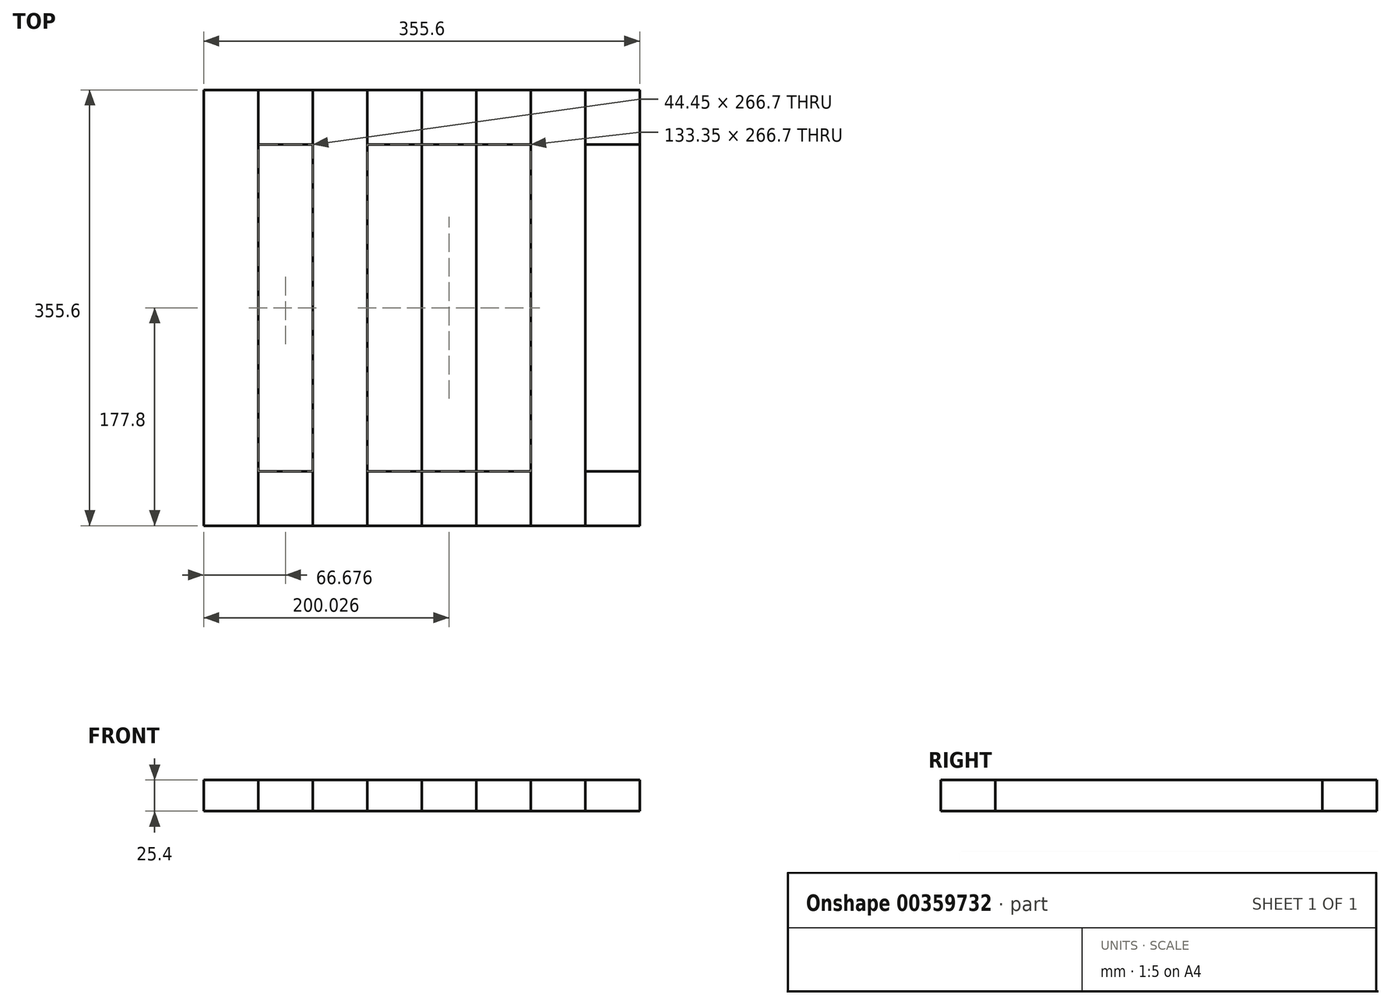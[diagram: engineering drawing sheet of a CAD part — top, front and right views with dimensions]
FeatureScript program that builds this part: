
annotation { "Feature Type Name" : "Feature", "Feature Type Description" : "" }
export const myFeature = defineFeature(function(context is Context, id is Id, definition is map)
    precondition{}
    {
        {
            var Q0;
            Q0=qCreatedBy(makeId("Top.planeOp"),FACE);
            var sketch = newSketch(context, id + "F0", { "sketchPlane" : qUnion([Q0])});
            skLineSegment(sketch, "E0.bottom", {"start": v(181.84, 177.8) * mm, "end": v(-173.76, 177.8) * mm});
            skLineSegment(sketch, "E0.top", {"start": v(181.84, -177.8) * mm, "end": v(-173.76, -177.8) * mm});
            skLineSegment(sketch, "E0.left", {"start": v(181.84, 177.8) * mm, "end": v(181.84, -177.8) * mm});
            skLineSegment(sketch, "E0.right", {"start": v(-173.76, 177.8) * mm, "end": v(-173.76, -177.8) * mm});
            skPoint(sketch, "E0.middle", {"position": v(4.04, 0) * mm});
            skLineSegment(sketch, "E1", {"start": v(-129.3, 177.8) * mm, "end": v(-129.3, -177.8) * mm});
            skLineSegment(sketch, "E2", {"start": v(-84.86, -177.8) * mm, "end": v(-84.86, 177.8) * mm});
            skLineSegment(sketch, "E3", {"start": v(-40.4, -177.8) * mm, "end": v(-40.4, 177.8) * mm});
            skLineSegment(sketch, "E4", {"start": v(4.04, 177.8) * mm, "end": v(4.04, -177.8) * mm});
            skLineSegment(sketch, "E5", {"start": v(4.04, -177.8) * mm, "end": v(4.04, 177.8) * mm});
            skLineSegment(sketch, "E6.MirrorCS", {"start": v(48.5, -177.8) * mm, "end": v(48.5, 177.8) * mm});
            skLineSegment(sketch, "E7.MirrorCS", {"start": v(92.94, -177.8) * mm, "end": v(92.94, 177.8) * mm});
            skLineSegment(sketch, "E8.MirrorCS", {"start": v(137.4, 177.8) * mm, "end": v(137.4, -177.8) * mm});
            skLineSegment(sketch, "E9", {"start": v(4.04, 0) * mm, "end": v(-173.76, 0) * mm});
            skLineSegment(sketch, "E10", {"start": v(-173.76, 0) * mm, "end": v(181.84, 0) * mm});
            skLineSegment(sketch, "E11", {"start": v(-173.76, 44.45) * mm, "end": v(181.84, 44.45) * mm});
            skLineSegment(sketch, "E12", {"start": v(181.84, 88.9) * mm, "end": v(-173.76, 88.9) * mm});
            skLineSegment(sketch, "E13", {"start": v(-173.76, 133.35) * mm, "end": v(181.84, 133.35) * mm});
            skLineSegment(sketch, "E14.MirrorCS", {"start": v(-173.76, -44.45) * mm, "end": v(181.84, -44.45) * mm});
            skLineSegment(sketch, "E15.MirrorCS", {"start": v(181.84, -88.9) * mm, "end": v(-173.76, -88.9) * mm});
            skLineSegment(sketch, "E16.MirrorCS", {"start": v(-173.76, -133.35) * mm, "end": v(181.84, -133.35) * mm});
            skSolve(sketch);
        }
        {
            var Q0;
            {var subQ0=sQuery(id+"F0.wireOp",EDGE,"E0.right");var subQ1=sQuery(id+"F0.wireOp",EDGE,"E0.bottom");var subQ2=makeQuery(id+"F0.imprint","INTERSECT",VERTEX,{"derivedFrom":[subQ1,subQ0]});Q0=makeQuery(id+"F0.imprint","IMPRINT",FACE,{"disambiguationData":[TD([[makeQuery(id+"F0.imprint","IMPRINT",EDGE,{"disambiguationData":[TD([[subQ2,1.0]])],"derivedFrom":subQ1}),1.0]])]});}
            var Q1;
            {var subQ0=sQuery(id+"F0.wireOp",EDGE,"E12");var subQ1=sQuery(id+"F0.wireOp",EDGE,"E0.right");var subQ2=makeQuery(id+"F0.imprint","INTERSECT",VERTEX,{"derivedFrom":[subQ1,subQ0]});Q1=makeQuery(id+"F0.imprint","IMPRINT",FACE,{"disambiguationData":[TD([[makeQuery(id+"F0.imprint","IMPRINT",EDGE,{"disambiguationData":[TD([[subQ2,1.0]])],"derivedFrom":subQ1}),1.0]])]});}
            var Q2;
            {var subQ0=sQuery(id+"F0.wireOp",EDGE,"E11");var subQ1=sQuery(id+"F0.wireOp",EDGE,"E0.right");var subQ2=makeQuery(id+"F0.imprint","INTERSECT",VERTEX,{"derivedFrom":[subQ1,subQ0]});Q2=makeQuery(id+"F0.imprint","IMPRINT",FACE,{"disambiguationData":[TD([[makeQuery(id+"F0.imprint","IMPRINT",EDGE,{"disambiguationData":[TD([[subQ2,1.0]])],"derivedFrom":subQ1}),1.0]])]});}
            var Q3;
            {var subQ0=sQuery(id+"F0.wireOp",EDGE,"E10");var subQ1=sQuery(id+"F0.wireOp",EDGE,"E0.right");var subQ2=makeQuery(id+"F0.imprint","INTERSECT",VERTEX,{"derivedFrom":[subQ1,subQ0]});Q3=makeQuery(id+"F0.imprint","IMPRINT",FACE,{"disambiguationData":[TD([[makeQuery(id+"F0.imprint","IMPRINT",EDGE,{"disambiguationData":[TD([[subQ2,-1.0]])],"derivedFrom":subQ1}),1.0]])]});}
            var Q4;
            {var subQ0=sQuery(id+"F0.wireOp",EDGE,"E14.MirrorCS");var subQ1=sQuery(id+"F0.wireOp",EDGE,"E0.right");var subQ2=makeQuery(id+"F0.imprint","INTERSECT",VERTEX,{"derivedFrom":[subQ1,subQ0]});Q4=makeQuery(id+"F0.imprint","IMPRINT",FACE,{"disambiguationData":[TD([[makeQuery(id+"F0.imprint","IMPRINT",EDGE,{"disambiguationData":[TD([[subQ2,-1.0]])],"derivedFrom":subQ1}),1.0]])]});}
            var Q5;
            {var subQ0=sQuery(id+"F0.wireOp",EDGE,"E10");var subQ1=sQuery(id+"F0.wireOp",EDGE,"E0.right");var subQ2=makeQuery(id+"F0.imprint","INTERSECT",VERTEX,{"derivedFrom":[subQ1,subQ0]});Q5=makeQuery(id+"F0.imprint","IMPRINT",FACE,{"disambiguationData":[TD([[makeQuery(id+"F0.imprint","IMPRINT",EDGE,{"disambiguationData":[TD([[subQ2,1.0]])],"derivedFrom":subQ1}),1.0]])]});}
            var Q6;
            {var subQ0=sQuery(id+"F0.wireOp",EDGE,"E15.MirrorCS");var subQ1=sQuery(id+"F0.wireOp",EDGE,"E0.right");var subQ2=makeQuery(id+"F0.imprint","INTERSECT",VERTEX,{"derivedFrom":[subQ1,subQ0]});Q6=makeQuery(id+"F0.imprint","IMPRINT",FACE,{"disambiguationData":[TD([[makeQuery(id+"F0.imprint","IMPRINT",EDGE,{"disambiguationData":[TD([[subQ2,-1.0]])],"derivedFrom":subQ1}),1.0]])]});}
            var Q7;
            {var subQ0=sQuery(id+"F0.wireOp",EDGE,"E0.right");var subQ1=sQuery(id+"F0.wireOp",EDGE,"E0.top");var subQ2=makeQuery(id+"F0.imprint","INTERSECT",VERTEX,{"derivedFrom":[subQ1,subQ0]});Q7=makeQuery(id+"F0.imprint","IMPRINT",FACE,{"disambiguationData":[TD([[makeQuery(id+"F0.imprint","IMPRINT",EDGE,{"disambiguationData":[TD([[subQ2,1.0]])],"derivedFrom":subQ1}),-1.0]])]});}
            var Q8;
            {var subQ0=sQuery(id+"F0.wireOp",EDGE,"E2");var subQ1=sQuery(id+"F0.wireOp",EDGE,"E0.top");var subQ2=makeQuery(id+"F0.imprint","INTERSECT",VERTEX,{"derivedFrom":[subQ1,subQ0]});Q8=makeQuery(id+"F0.imprint","IMPRINT",FACE,{"disambiguationData":[TD([[makeQuery(id+"F0.imprint","IMPRINT",EDGE,{"disambiguationData":[TD([[subQ2,1.0]])],"derivedFrom":subQ1}),-1.0]])]});}
            var Q9;
            {var subQ0=sQuery(id+"F0.wireOp",EDGE,"E16.MirrorCS");var subQ1=sQuery(id+"F0.wireOp",EDGE,"E2");var subQ2=makeQuery(id+"F0.imprint","INTERSECT",VERTEX,{"derivedFrom":[subQ1,subQ0]});Q9=makeQuery(id+"F0.imprint","IMPRINT",FACE,{"disambiguationData":[TD([[makeQuery(id+"F0.imprint","IMPRINT",EDGE,{"disambiguationData":[TD([[subQ2,-1.0]])],"derivedFrom":subQ1}),-1.0]])]});}
            var Q10;
            {var subQ0=sQuery(id+"F0.wireOp",EDGE,"E15.MirrorCS");var subQ1=sQuery(id+"F0.wireOp",EDGE,"E2");var subQ2=makeQuery(id+"F0.imprint","INTERSECT",VERTEX,{"derivedFrom":[subQ1,subQ0]});Q10=makeQuery(id+"F0.imprint","IMPRINT",FACE,{"disambiguationData":[TD([[makeQuery(id+"F0.imprint","IMPRINT",EDGE,{"disambiguationData":[TD([[subQ2,-1.0]])],"derivedFrom":subQ1}),-1.0]])]});}
            var Q11;
            {var subQ0=sQuery(id+"F0.wireOp",EDGE,"E14.MirrorCS");var subQ1=sQuery(id+"F0.wireOp",EDGE,"E2");var subQ2=makeQuery(id+"F0.imprint","INTERSECT",VERTEX,{"derivedFrom":[subQ1,subQ0]});Q11=makeQuery(id+"F0.imprint","IMPRINT",FACE,{"disambiguationData":[TD([[makeQuery(id+"F0.imprint","IMPRINT",EDGE,{"disambiguationData":[TD([[subQ2,-1.0]])],"derivedFrom":subQ1}),-1.0]])]});}
            var Q12;
            {var subQ0=sQuery(id+"F0.wireOp",EDGE,"E10");var subQ1=sQuery(id+"F0.wireOp",EDGE,"E2");var subQ2=makeQuery(id+"F0.imprint","INTERSECT",VERTEX,{"derivedFrom":[subQ1,subQ0]});Q12=makeQuery(id+"F0.imprint","IMPRINT",FACE,{"disambiguationData":[TD([[makeQuery(id+"F0.imprint","IMPRINT",EDGE,{"disambiguationData":[TD([[subQ2,-1.0]])],"derivedFrom":subQ1}),-1.0]])]});}
            var Q13;
            {var subQ0=sQuery(id+"F0.wireOp",EDGE,"E11");var subQ1=sQuery(id+"F0.wireOp",EDGE,"E2");var subQ2=makeQuery(id+"F0.imprint","INTERSECT",VERTEX,{"derivedFrom":[subQ1,subQ0]});Q13=makeQuery(id+"F0.imprint","IMPRINT",FACE,{"disambiguationData":[TD([[makeQuery(id+"F0.imprint","IMPRINT",EDGE,{"disambiguationData":[TD([[subQ2,-1.0]])],"derivedFrom":subQ1}),-1.0]])]});}
            var Q14;
            {var subQ0=sQuery(id+"F0.wireOp",EDGE,"E12");var subQ1=sQuery(id+"F0.wireOp",EDGE,"E2");var subQ2=makeQuery(id+"F0.imprint","INTERSECT",VERTEX,{"derivedFrom":[subQ1,subQ0]});Q14=makeQuery(id+"F0.imprint","IMPRINT",FACE,{"disambiguationData":[TD([[makeQuery(id+"F0.imprint","IMPRINT",EDGE,{"disambiguationData":[TD([[subQ2,-1.0]])],"derivedFrom":subQ1}),-1.0]])]});}
            var Q15;
            {var subQ0=sQuery(id+"F0.wireOp",EDGE,"E2");var subQ1=sQuery(id+"F0.wireOp",EDGE,"E0.bottom");var subQ2=makeQuery(id+"F0.imprint","INTERSECT",VERTEX,{"derivedFrom":[subQ1,subQ0]});Q15=makeQuery(id+"F0.imprint","IMPRINT",FACE,{"disambiguationData":[TD([[makeQuery(id+"F0.imprint","IMPRINT",EDGE,{"disambiguationData":[TD([[subQ2,1.0]])],"derivedFrom":subQ1}),1.0]])]});}
            var Q16;
            {var subQ0=sQuery(id+"F0.wireOp",EDGE,"E4");var subQ1=sQuery(id+"F0.wireOp",EDGE,"E0.bottom");var subQ2=makeQuery(id+"F0.imprint","INTERSECT",VERTEX,{"derivedFrom":[subQ1,subQ0]});Q16=makeQuery(id+"F0.imprint","IMPRINT",FACE,{"disambiguationData":[TD([[makeQuery(id+"F0.imprint","IMPRINT",EDGE,{"disambiguationData":[TD([[subQ2,1.0]])],"derivedFrom":subQ1}),1.0]])]});}
            var Q17;
            {var subQ0=sQuery(id+"F0.wireOp",EDGE,"E13");var subQ1=sQuery(id+"F0.wireOp",EDGE,"E4");var subQ2=makeQuery(id+"F0.imprint","INTERSECT",VERTEX,{"derivedFrom":[subQ1,subQ0]});Q17=makeQuery(id+"F0.imprint","IMPRINT",FACE,{"disambiguationData":[TD([[makeQuery(id+"F0.imprint","IMPRINT",EDGE,{"disambiguationData":[TD([[subQ2,-1.0]])],"derivedFrom":subQ1}),1.0]])]});}
            var Q18;
            {var subQ0=sQuery(id+"F0.wireOp",EDGE,"E12");var subQ1=sQuery(id+"F0.wireOp",EDGE,"E4");var subQ2=makeQuery(id+"F0.imprint","INTERSECT",VERTEX,{"derivedFrom":[subQ1,subQ0]});Q18=makeQuery(id+"F0.imprint","IMPRINT",FACE,{"disambiguationData":[TD([[makeQuery(id+"F0.imprint","IMPRINT",EDGE,{"disambiguationData":[TD([[subQ2,-1.0]])],"derivedFrom":subQ1}),1.0]])]});}
            var Q19;
            {var subQ0=sQuery(id+"F0.wireOp",EDGE,"E11");var subQ1=sQuery(id+"F0.wireOp",EDGE,"E4");var subQ2=makeQuery(id+"F0.imprint","INTERSECT",VERTEX,{"derivedFrom":[subQ1,subQ0]});Q19=makeQuery(id+"F0.imprint","IMPRINT",FACE,{"disambiguationData":[TD([[makeQuery(id+"F0.imprint","IMPRINT",EDGE,{"disambiguationData":[TD([[subQ2,-1.0]])],"derivedFrom":subQ1}),1.0]])]});}
            var Q20;
            {var subQ0=sQuery(id+"F0.wireOp",EDGE,"E10");var subQ1=sQuery(id+"F0.wireOp",EDGE,"E4");var subQ2=makeQuery(id+"F0.imprint","INTERSECT",VERTEX,{"derivedFrom":[subQ1,subQ0]});Q20=makeQuery(id+"F0.imprint","IMPRINT",FACE,{"disambiguationData":[TD([[makeQuery(id+"F0.imprint","IMPRINT",EDGE,{"disambiguationData":[TD([[subQ2,-1.0]])],"derivedFrom":subQ1}),1.0]])]});}
            var Q21;
            {var subQ0=sQuery(id+"F0.wireOp",EDGE,"E14.MirrorCS");var subQ1=sQuery(id+"F0.wireOp",EDGE,"E4");var subQ2=makeQuery(id+"F0.imprint","INTERSECT",VERTEX,{"derivedFrom":[subQ1,subQ0]});Q21=makeQuery(id+"F0.imprint","IMPRINT",FACE,{"disambiguationData":[TD([[makeQuery(id+"F0.imprint","IMPRINT",EDGE,{"disambiguationData":[TD([[subQ2,-1.0]])],"derivedFrom":subQ1}),1.0]])]});}
            var Q22;
            {var subQ0=sQuery(id+"F0.wireOp",EDGE,"E15.MirrorCS");var subQ1=sQuery(id+"F0.wireOp",EDGE,"E4");var subQ2=makeQuery(id+"F0.imprint","INTERSECT",VERTEX,{"derivedFrom":[subQ1,subQ0]});Q22=makeQuery(id+"F0.imprint","IMPRINT",FACE,{"disambiguationData":[TD([[makeQuery(id+"F0.imprint","IMPRINT",EDGE,{"disambiguationData":[TD([[subQ2,-1.0]])],"derivedFrom":subQ1}),1.0]])]});}
            var Q23;
            {var subQ0=sQuery(id+"F0.wireOp",EDGE,"E4");var subQ1=sQuery(id+"F0.wireOp",EDGE,"E0.top");var subQ2=makeQuery(id+"F0.imprint","INTERSECT",VERTEX,{"derivedFrom":[subQ1,subQ0]});Q23=makeQuery(id+"F0.imprint","IMPRINT",FACE,{"disambiguationData":[TD([[makeQuery(id+"F0.imprint","IMPRINT",EDGE,{"disambiguationData":[TD([[subQ2,1.0]])],"derivedFrom":subQ1}),-1.0]])]});}
            var Q24;
            {var subQ0=sQuery(id+"F0.wireOp",EDGE,"E7.MirrorCS");var subQ1=sQuery(id+"F0.wireOp",EDGE,"E0.top");var subQ2=makeQuery(id+"F0.imprint","INTERSECT",VERTEX,{"derivedFrom":[subQ1,subQ0]});Q24=makeQuery(id+"F0.imprint","IMPRINT",FACE,{"disambiguationData":[TD([[makeQuery(id+"F0.imprint","IMPRINT",EDGE,{"disambiguationData":[TD([[subQ2,1.0]])],"derivedFrom":subQ1}),-1.0]])]});}
            var Q25;
            {var subQ0=sQuery(id+"F0.wireOp",EDGE,"E16.MirrorCS");var subQ1=sQuery(id+"F0.wireOp",EDGE,"E7.MirrorCS");var subQ2=makeQuery(id+"F0.imprint","INTERSECT",VERTEX,{"derivedFrom":[subQ1,subQ0]});Q25=makeQuery(id+"F0.imprint","IMPRINT",FACE,{"disambiguationData":[TD([[makeQuery(id+"F0.imprint","IMPRINT",EDGE,{"disambiguationData":[TD([[subQ2,-1.0]])],"derivedFrom":subQ1}),-1.0]])]});}
            var Q26;
            {var subQ0=sQuery(id+"F0.wireOp",EDGE,"E15.MirrorCS");var subQ1=sQuery(id+"F0.wireOp",EDGE,"E7.MirrorCS");var subQ2=makeQuery(id+"F0.imprint","INTERSECT",VERTEX,{"derivedFrom":[subQ1,subQ0]});Q26=makeQuery(id+"F0.imprint","IMPRINT",FACE,{"disambiguationData":[TD([[makeQuery(id+"F0.imprint","IMPRINT",EDGE,{"disambiguationData":[TD([[subQ2,-1.0]])],"derivedFrom":subQ1}),-1.0]])]});}
            var Q27;
            {var subQ0=sQuery(id+"F0.wireOp",EDGE,"E14.MirrorCS");var subQ1=sQuery(id+"F0.wireOp",EDGE,"E7.MirrorCS");var subQ2=makeQuery(id+"F0.imprint","INTERSECT",VERTEX,{"derivedFrom":[subQ1,subQ0]});Q27=makeQuery(id+"F0.imprint","IMPRINT",FACE,{"disambiguationData":[TD([[makeQuery(id+"F0.imprint","IMPRINT",EDGE,{"disambiguationData":[TD([[subQ2,-1.0]])],"derivedFrom":subQ1}),-1.0]])]});}
            var Q28;
            {var subQ0=sQuery(id+"F0.wireOp",EDGE,"E10");var subQ1=sQuery(id+"F0.wireOp",EDGE,"E7.MirrorCS");var subQ2=makeQuery(id+"F0.imprint","INTERSECT",VERTEX,{"derivedFrom":[subQ1,subQ0]});Q28=makeQuery(id+"F0.imprint","IMPRINT",FACE,{"disambiguationData":[TD([[makeQuery(id+"F0.imprint","IMPRINT",EDGE,{"disambiguationData":[TD([[subQ2,-1.0]])],"derivedFrom":subQ1}),-1.0]])]});}
            var Q29;
            {var subQ0=sQuery(id+"F0.wireOp",EDGE,"E11");var subQ1=sQuery(id+"F0.wireOp",EDGE,"E7.MirrorCS");var subQ2=makeQuery(id+"F0.imprint","INTERSECT",VERTEX,{"derivedFrom":[subQ1,subQ0]});Q29=makeQuery(id+"F0.imprint","IMPRINT",FACE,{"disambiguationData":[TD([[makeQuery(id+"F0.imprint","IMPRINT",EDGE,{"disambiguationData":[TD([[subQ2,-1.0]])],"derivedFrom":subQ1}),-1.0]])]});}
            var Q30;
            {var subQ0=sQuery(id+"F0.wireOp",EDGE,"E12");var subQ1=sQuery(id+"F0.wireOp",EDGE,"E7.MirrorCS");var subQ2=makeQuery(id+"F0.imprint","INTERSECT",VERTEX,{"derivedFrom":[subQ1,subQ0]});Q30=makeQuery(id+"F0.imprint","IMPRINT",FACE,{"disambiguationData":[TD([[makeQuery(id+"F0.imprint","IMPRINT",EDGE,{"disambiguationData":[TD([[subQ2,-1.0]])],"derivedFrom":subQ1}),-1.0]])]});}
            var Q31;
            {var subQ0=sQuery(id+"F0.wireOp",EDGE,"E7.MirrorCS");var subQ1=sQuery(id+"F0.wireOp",EDGE,"E0.bottom");var subQ2=makeQuery(id+"F0.imprint","INTERSECT",VERTEX,{"derivedFrom":[subQ1,subQ0]});Q31=makeQuery(id+"F0.imprint","IMPRINT",FACE,{"disambiguationData":[TD([[makeQuery(id+"F0.imprint","IMPRINT",EDGE,{"disambiguationData":[TD([[subQ2,1.0]])],"derivedFrom":subQ1}),1.0]])]});}
            extrude(context, id + "F1", {"entities" : qUnion([Q0, Q1, Q2, Q3, Q4, Q5, Q6, Q7, Q8, Q9, Q10, Q11, Q12, Q13, Q14, Q15, Q16, Q17, Q18, Q19, Q20, Q21, Q22, Q23, Q24, Q25, Q26, Q27, Q28, Q29, Q30, Q31]), "depth" : 25.4 * mm});
        }
        {
            var Q0;
            {var subQ0=sQuery(id+"F0.wireOp",EDGE,"E1");var subQ1=sQuery(id+"F0.wireOp",EDGE,"E0.bottom");var subQ2=makeQuery(id+"F0.imprint","INTERSECT",VERTEX,{"derivedFrom":[subQ1,subQ0]});Q0=makeQuery(id+"F0.imprint","IMPRINT",FACE,{"disambiguationData":[TD([[makeQuery(id+"F0.imprint","IMPRINT",EDGE,{"disambiguationData":[TD([[subQ2,1.0]])],"derivedFrom":subQ1}),1.0]])]});}
            var Q1;
            {var subQ0=sQuery(id+"F0.wireOp",EDGE,"E13");var subQ1=sQuery(id+"F0.wireOp",EDGE,"E1");var subQ2=makeQuery(id+"F0.imprint","INTERSECT",VERTEX,{"derivedFrom":[subQ1,subQ0]});Q1=makeQuery(id+"F0.imprint","IMPRINT",FACE,{"disambiguationData":[TD([[makeQuery(id+"F0.imprint","IMPRINT",EDGE,{"disambiguationData":[TD([[subQ2,-1.0]])],"derivedFrom":subQ1}),1.0]])]});}
            var Q2;
            {var subQ0=sQuery(id+"F0.wireOp",EDGE,"E12");var subQ1=sQuery(id+"F0.wireOp",EDGE,"E1");var subQ2=makeQuery(id+"F0.imprint","INTERSECT",VERTEX,{"derivedFrom":[subQ1,subQ0]});Q2=makeQuery(id+"F0.imprint","IMPRINT",FACE,{"disambiguationData":[TD([[makeQuery(id+"F0.imprint","IMPRINT",EDGE,{"disambiguationData":[TD([[subQ2,-1.0]])],"derivedFrom":subQ1}),1.0]])]});}
            var Q3;
            {var subQ0=sQuery(id+"F0.wireOp",EDGE,"E11");var subQ1=sQuery(id+"F0.wireOp",EDGE,"E1");var subQ2=makeQuery(id+"F0.imprint","INTERSECT",VERTEX,{"derivedFrom":[subQ1,subQ0]});Q3=makeQuery(id+"F0.imprint","IMPRINT",FACE,{"disambiguationData":[TD([[makeQuery(id+"F0.imprint","IMPRINT",EDGE,{"disambiguationData":[TD([[subQ2,-1.0]])],"derivedFrom":subQ1}),1.0]])]});}
            var Q4;
            {var subQ0=sQuery(id+"F0.wireOp",EDGE,"E10");var subQ1=sQuery(id+"F0.wireOp",EDGE,"E1");var subQ2=makeQuery(id+"F0.imprint","INTERSECT",VERTEX,{"derivedFrom":[subQ1,subQ0]});Q4=makeQuery(id+"F0.imprint","IMPRINT",FACE,{"disambiguationData":[TD([[makeQuery(id+"F0.imprint","IMPRINT",EDGE,{"disambiguationData":[TD([[subQ2,-1.0]])],"derivedFrom":subQ1}),1.0]])]});}
            var Q5;
            {var subQ0=sQuery(id+"F0.wireOp",EDGE,"E14.MirrorCS");var subQ1=sQuery(id+"F0.wireOp",EDGE,"E1");var subQ2=makeQuery(id+"F0.imprint","INTERSECT",VERTEX,{"derivedFrom":[subQ1,subQ0]});Q5=makeQuery(id+"F0.imprint","IMPRINT",FACE,{"disambiguationData":[TD([[makeQuery(id+"F0.imprint","IMPRINT",EDGE,{"disambiguationData":[TD([[subQ2,-1.0]])],"derivedFrom":subQ1}),1.0]])]});}
            var Q6;
            {var subQ0=sQuery(id+"F0.wireOp",EDGE,"E15.MirrorCS");var subQ1=sQuery(id+"F0.wireOp",EDGE,"E1");var subQ2=makeQuery(id+"F0.imprint","INTERSECT",VERTEX,{"derivedFrom":[subQ1,subQ0]});Q6=makeQuery(id+"F0.imprint","IMPRINT",FACE,{"disambiguationData":[TD([[makeQuery(id+"F0.imprint","IMPRINT",EDGE,{"disambiguationData":[TD([[subQ2,-1.0]])],"derivedFrom":subQ1}),1.0]])]});}
            var Q7;
            {var subQ0=sQuery(id+"F0.wireOp",EDGE,"E1");var subQ1=sQuery(id+"F0.wireOp",EDGE,"E0.top");var subQ2=makeQuery(id+"F0.imprint","INTERSECT",VERTEX,{"derivedFrom":[subQ1,subQ0]});Q7=makeQuery(id+"F0.imprint","IMPRINT",FACE,{"disambiguationData":[TD([[makeQuery(id+"F0.imprint","IMPRINT",EDGE,{"disambiguationData":[TD([[subQ2,1.0]])],"derivedFrom":subQ1}),-1.0]])]});}
            var Q8;
            {var subQ0=sQuery(id+"F0.wireOp",EDGE,"E3");var subQ1=sQuery(id+"F0.wireOp",EDGE,"E0.top");var subQ2=makeQuery(id+"F0.imprint","INTERSECT",VERTEX,{"derivedFrom":[subQ1,subQ0]});Q8=makeQuery(id+"F0.imprint","IMPRINT",FACE,{"disambiguationData":[TD([[makeQuery(id+"F0.imprint","IMPRINT",EDGE,{"disambiguationData":[TD([[subQ2,1.0]])],"derivedFrom":subQ1}),-1.0]])]});}
            var Q9;
            {var subQ0=sQuery(id+"F0.wireOp",EDGE,"E16.MirrorCS");var subQ1=sQuery(id+"F0.wireOp",EDGE,"E3");var subQ2=makeQuery(id+"F0.imprint","INTERSECT",VERTEX,{"derivedFrom":[subQ1,subQ0]});Q9=makeQuery(id+"F0.imprint","IMPRINT",FACE,{"disambiguationData":[TD([[makeQuery(id+"F0.imprint","IMPRINT",EDGE,{"disambiguationData":[TD([[subQ2,-1.0]])],"derivedFrom":subQ1}),-1.0]])]});}
            var Q10;
            {var subQ0=sQuery(id+"F0.wireOp",EDGE,"E15.MirrorCS");var subQ1=sQuery(id+"F0.wireOp",EDGE,"E3");var subQ2=makeQuery(id+"F0.imprint","INTERSECT",VERTEX,{"derivedFrom":[subQ1,subQ0]});Q10=makeQuery(id+"F0.imprint","IMPRINT",FACE,{"disambiguationData":[TD([[makeQuery(id+"F0.imprint","IMPRINT",EDGE,{"disambiguationData":[TD([[subQ2,-1.0]])],"derivedFrom":subQ1}),-1.0]])]});}
            var Q11;
            {var subQ0=sQuery(id+"F0.wireOp",EDGE,"E14.MirrorCS");var subQ1=sQuery(id+"F0.wireOp",EDGE,"E3");var subQ2=makeQuery(id+"F0.imprint","INTERSECT",VERTEX,{"derivedFrom":[subQ1,subQ0]});Q11=makeQuery(id+"F0.imprint","IMPRINT",FACE,{"disambiguationData":[TD([[makeQuery(id+"F0.imprint","IMPRINT",EDGE,{"disambiguationData":[TD([[subQ2,-1.0]])],"derivedFrom":subQ1}),-1.0]])]});}
            var Q12;
            {var subQ0=sQuery(id+"F0.wireOp",EDGE,"E10");var subQ1=sQuery(id+"F0.wireOp",EDGE,"E3");var subQ2=makeQuery(id+"F0.imprint","INTERSECT",VERTEX,{"derivedFrom":[subQ1,subQ0]});Q12=makeQuery(id+"F0.imprint","IMPRINT",FACE,{"disambiguationData":[TD([[makeQuery(id+"F0.imprint","IMPRINT",EDGE,{"disambiguationData":[TD([[subQ2,-1.0]])],"derivedFrom":subQ1}),-1.0]])]});}
            var Q13;
            {var subQ0=sQuery(id+"F0.wireOp",EDGE,"E11");var subQ1=sQuery(id+"F0.wireOp",EDGE,"E3");var subQ2=makeQuery(id+"F0.imprint","INTERSECT",VERTEX,{"derivedFrom":[subQ1,subQ0]});Q13=makeQuery(id+"F0.imprint","IMPRINT",FACE,{"disambiguationData":[TD([[makeQuery(id+"F0.imprint","IMPRINT",EDGE,{"disambiguationData":[TD([[subQ2,-1.0]])],"derivedFrom":subQ1}),-1.0]])]});}
            var Q14;
            {var subQ0=sQuery(id+"F0.wireOp",EDGE,"E12");var subQ1=sQuery(id+"F0.wireOp",EDGE,"E3");var subQ2=makeQuery(id+"F0.imprint","INTERSECT",VERTEX,{"derivedFrom":[subQ1,subQ0]});Q14=makeQuery(id+"F0.imprint","IMPRINT",FACE,{"disambiguationData":[TD([[makeQuery(id+"F0.imprint","IMPRINT",EDGE,{"disambiguationData":[TD([[subQ2,-1.0]])],"derivedFrom":subQ1}),-1.0]])]});}
            var Q15;
            {var subQ0=sQuery(id+"F0.wireOp",EDGE,"E3");var subQ1=sQuery(id+"F0.wireOp",EDGE,"E0.bottom");var subQ2=makeQuery(id+"F0.imprint","INTERSECT",VERTEX,{"derivedFrom":[subQ1,subQ0]});Q15=makeQuery(id+"F0.imprint","IMPRINT",FACE,{"disambiguationData":[TD([[makeQuery(id+"F0.imprint","IMPRINT",EDGE,{"disambiguationData":[TD([[subQ2,1.0]])],"derivedFrom":subQ1}),1.0]])]});}
            var Q16;
            {var subQ0=sQuery(id+"F0.wireOp",EDGE,"E6.MirrorCS");var subQ1=sQuery(id+"F0.wireOp",EDGE,"E0.bottom");var subQ2=makeQuery(id+"F0.imprint","INTERSECT",VERTEX,{"derivedFrom":[subQ1,subQ0]});Q16=makeQuery(id+"F0.imprint","IMPRINT",FACE,{"disambiguationData":[TD([[makeQuery(id+"F0.imprint","IMPRINT",EDGE,{"disambiguationData":[TD([[subQ2,1.0]])],"derivedFrom":subQ1}),1.0]])]});}
            var Q17;
            {var subQ0=sQuery(id+"F0.wireOp",EDGE,"E12");var subQ1=sQuery(id+"F0.wireOp",EDGE,"E6.MirrorCS");var subQ2=makeQuery(id+"F0.imprint","INTERSECT",VERTEX,{"derivedFrom":[subQ1,subQ0]});Q17=makeQuery(id+"F0.imprint","IMPRINT",FACE,{"disambiguationData":[TD([[makeQuery(id+"F0.imprint","IMPRINT",EDGE,{"disambiguationData":[TD([[subQ2,-1.0]])],"derivedFrom":subQ1}),-1.0]])]});}
            var Q18;
            {var subQ0=sQuery(id+"F0.wireOp",EDGE,"E11");var subQ1=sQuery(id+"F0.wireOp",EDGE,"E6.MirrorCS");var subQ2=makeQuery(id+"F0.imprint","INTERSECT",VERTEX,{"derivedFrom":[subQ1,subQ0]});Q18=makeQuery(id+"F0.imprint","IMPRINT",FACE,{"disambiguationData":[TD([[makeQuery(id+"F0.imprint","IMPRINT",EDGE,{"disambiguationData":[TD([[subQ2,-1.0]])],"derivedFrom":subQ1}),-1.0]])]});}
            var Q19;
            {var subQ0=sQuery(id+"F0.wireOp",EDGE,"E10");var subQ1=sQuery(id+"F0.wireOp",EDGE,"E6.MirrorCS");var subQ2=makeQuery(id+"F0.imprint","INTERSECT",VERTEX,{"derivedFrom":[subQ1,subQ0]});Q19=makeQuery(id+"F0.imprint","IMPRINT",FACE,{"disambiguationData":[TD([[makeQuery(id+"F0.imprint","IMPRINT",EDGE,{"disambiguationData":[TD([[subQ2,-1.0]])],"derivedFrom":subQ1}),-1.0]])]});}
            var Q20;
            {var subQ0=sQuery(id+"F0.wireOp",EDGE,"E14.MirrorCS");var subQ1=sQuery(id+"F0.wireOp",EDGE,"E6.MirrorCS");var subQ2=makeQuery(id+"F0.imprint","INTERSECT",VERTEX,{"derivedFrom":[subQ1,subQ0]});Q20=makeQuery(id+"F0.imprint","IMPRINT",FACE,{"disambiguationData":[TD([[makeQuery(id+"F0.imprint","IMPRINT",EDGE,{"disambiguationData":[TD([[subQ2,-1.0]])],"derivedFrom":subQ1}),-1.0]])]});}
            var Q21;
            {var subQ0=sQuery(id+"F0.wireOp",EDGE,"E15.MirrorCS");var subQ1=sQuery(id+"F0.wireOp",EDGE,"E6.MirrorCS");var subQ2=makeQuery(id+"F0.imprint","INTERSECT",VERTEX,{"derivedFrom":[subQ1,subQ0]});Q21=makeQuery(id+"F0.imprint","IMPRINT",FACE,{"disambiguationData":[TD([[makeQuery(id+"F0.imprint","IMPRINT",EDGE,{"disambiguationData":[TD([[subQ2,-1.0]])],"derivedFrom":subQ1}),-1.0]])]});}
            var Q22;
            {var subQ0=sQuery(id+"F0.wireOp",EDGE,"E16.MirrorCS");var subQ1=sQuery(id+"F0.wireOp",EDGE,"E6.MirrorCS");var subQ2=makeQuery(id+"F0.imprint","INTERSECT",VERTEX,{"derivedFrom":[subQ1,subQ0]});Q22=makeQuery(id+"F0.imprint","IMPRINT",FACE,{"disambiguationData":[TD([[makeQuery(id+"F0.imprint","IMPRINT",EDGE,{"disambiguationData":[TD([[subQ2,-1.0]])],"derivedFrom":subQ1}),-1.0]])]});}
            var Q23;
            {var subQ0=sQuery(id+"F0.wireOp",EDGE,"E6.MirrorCS");var subQ1=sQuery(id+"F0.wireOp",EDGE,"E0.top");var subQ2=makeQuery(id+"F0.imprint","INTERSECT",VERTEX,{"derivedFrom":[subQ1,subQ0]});Q23=makeQuery(id+"F0.imprint","IMPRINT",FACE,{"disambiguationData":[TD([[makeQuery(id+"F0.imprint","IMPRINT",EDGE,{"disambiguationData":[TD([[subQ2,1.0]])],"derivedFrom":subQ1}),-1.0]])]});}
            var Q24;
            {var subQ0=sQuery(id+"F0.wireOp",EDGE,"E0.left");var subQ1=sQuery(id+"F0.wireOp",EDGE,"E0.top");var subQ2=makeQuery(id+"F0.imprint","INTERSECT",VERTEX,{"derivedFrom":[subQ1,subQ0]});Q24=makeQuery(id+"F0.imprint","IMPRINT",FACE,{"disambiguationData":[TD([[makeQuery(id+"F0.imprint","IMPRINT",EDGE,{"disambiguationData":[TD([[subQ2,-1.0]])],"derivedFrom":subQ1}),-1.0]])]});}
            var Q25;
            {var subQ0=sQuery(id+"F0.wireOp",EDGE,"E15.MirrorCS");var subQ1=sQuery(id+"F0.wireOp",EDGE,"E0.left");var subQ2=makeQuery(id+"F0.imprint","INTERSECT",VERTEX,{"derivedFrom":[subQ1,subQ0]});Q25=makeQuery(id+"F0.imprint","IMPRINT",FACE,{"disambiguationData":[TD([[makeQuery(id+"F0.imprint","IMPRINT",EDGE,{"disambiguationData":[TD([[subQ2,-1.0]])],"derivedFrom":subQ1}),-1.0]])]});}
            var Q26;
            {var subQ0=sQuery(id+"F0.wireOp",EDGE,"E14.MirrorCS");var subQ1=sQuery(id+"F0.wireOp",EDGE,"E0.left");var subQ2=makeQuery(id+"F0.imprint","INTERSECT",VERTEX,{"derivedFrom":[subQ1,subQ0]});Q26=makeQuery(id+"F0.imprint","IMPRINT",FACE,{"disambiguationData":[TD([[makeQuery(id+"F0.imprint","IMPRINT",EDGE,{"disambiguationData":[TD([[subQ2,-1.0]])],"derivedFrom":subQ1}),-1.0]])]});}
            var Q27;
            {var subQ0=sQuery(id+"F0.wireOp",EDGE,"E10");var subQ1=sQuery(id+"F0.wireOp",EDGE,"E0.left");var subQ2=makeQuery(id+"F0.imprint","INTERSECT",VERTEX,{"derivedFrom":[subQ1,subQ0]});Q27=makeQuery(id+"F0.imprint","IMPRINT",FACE,{"disambiguationData":[TD([[makeQuery(id+"F0.imprint","IMPRINT",EDGE,{"disambiguationData":[TD([[subQ2,-1.0]])],"derivedFrom":subQ1}),-1.0]])]});}
            var Q28;
            {var subQ0=sQuery(id+"F0.wireOp",EDGE,"E10");var subQ1=sQuery(id+"F0.wireOp",EDGE,"E0.left");var subQ2=makeQuery(id+"F0.imprint","INTERSECT",VERTEX,{"derivedFrom":[subQ1,subQ0]});Q28=makeQuery(id+"F0.imprint","IMPRINT",FACE,{"disambiguationData":[TD([[makeQuery(id+"F0.imprint","IMPRINT",EDGE,{"disambiguationData":[TD([[subQ2,1.0]])],"derivedFrom":subQ1}),-1.0]])]});}
            var Q29;
            {var subQ0=sQuery(id+"F0.wireOp",EDGE,"E11");var subQ1=sQuery(id+"F0.wireOp",EDGE,"E0.left");var subQ2=makeQuery(id+"F0.imprint","INTERSECT",VERTEX,{"derivedFrom":[subQ1,subQ0]});Q29=makeQuery(id+"F0.imprint","IMPRINT",FACE,{"disambiguationData":[TD([[makeQuery(id+"F0.imprint","IMPRINT",EDGE,{"disambiguationData":[TD([[subQ2,1.0]])],"derivedFrom":subQ1}),-1.0]])]});}
            var Q30;
            {var subQ0=sQuery(id+"F0.wireOp",EDGE,"E12");var subQ1=sQuery(id+"F0.wireOp",EDGE,"E0.left");var subQ2=makeQuery(id+"F0.imprint","INTERSECT",VERTEX,{"derivedFrom":[subQ1,subQ0]});Q30=makeQuery(id+"F0.imprint","IMPRINT",FACE,{"disambiguationData":[TD([[makeQuery(id+"F0.imprint","IMPRINT",EDGE,{"disambiguationData":[TD([[subQ2,1.0]])],"derivedFrom":subQ1}),-1.0]])]});}
            var Q31;
            {var subQ0=sQuery(id+"F0.wireOp",EDGE,"E0.left");var subQ1=sQuery(id+"F0.wireOp",EDGE,"E0.bottom");var subQ2=makeQuery(id+"F0.imprint","INTERSECT",VERTEX,{"derivedFrom":[subQ1,subQ0]});Q31=makeQuery(id+"F0.imprint","IMPRINT",FACE,{"disambiguationData":[TD([[makeQuery(id+"F0.imprint","IMPRINT",EDGE,{"disambiguationData":[TD([[subQ2,-1.0]])],"derivedFrom":subQ1}),1.0]])]});}
            extrude(context, id + "F2", {"entities" : qUnion([Q0, Q1, Q2, Q3, Q4, Q5, Q6, Q7, Q8, Q9, Q10, Q11, Q12, Q13, Q14, Q15, Q16, Q17, Q18, Q19, Q20, Q21, Q22, Q23, Q24, Q25, Q26, Q27, Q28, Q29, Q30, Q31]), "depth" : 25.4 * mm});
        }
    });
